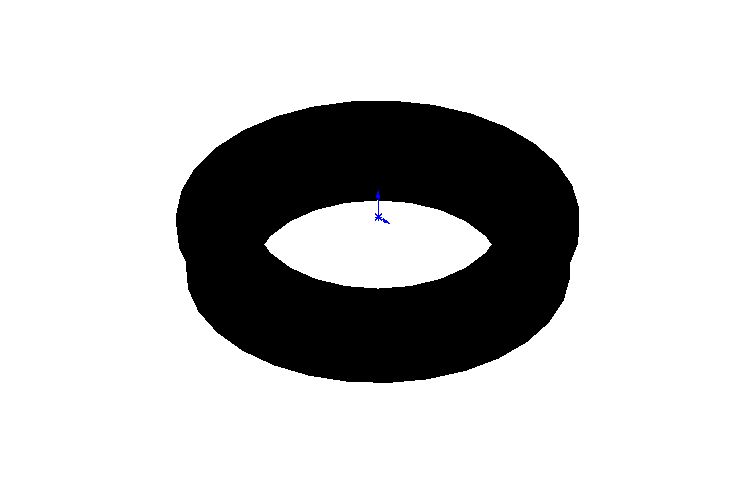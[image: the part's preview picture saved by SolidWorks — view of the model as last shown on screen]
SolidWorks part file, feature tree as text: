
SOLIDWORKS PART (.sldprt)
format: sldprt  version: not decoded by parser v0  size: 91,136 bytes
history: native  units: mm
features: plane x3, sketch x2, extrude x2, material x1, shell x1 (+10 scaffold rows collapsed)
feature tree (19):
  scaffold x10  (default folders/planes/origin — collapsed)
  material  "Matériau <non spécifié>"
  plane  "Plan de face"
  plane  "Plan de dessus"
  plane  "Plan de droite"
  sketch  "Esquisse1"  dims[D1=13.0mm D2=20.0mm]
  extrude  "Extrusion1"  Depth=3.5mm
  sketch  "Esquisse2"  dims[D1=21.0mm]
  extrude  "Extrusion2"  Depth=0.7mm
  shell  "Coque1"  Thickness=1mm
decode coverage: 5 of 5 modeling features carry decoded parameters
note: suppression state not decoded; provenance and decode notes live in map.json
